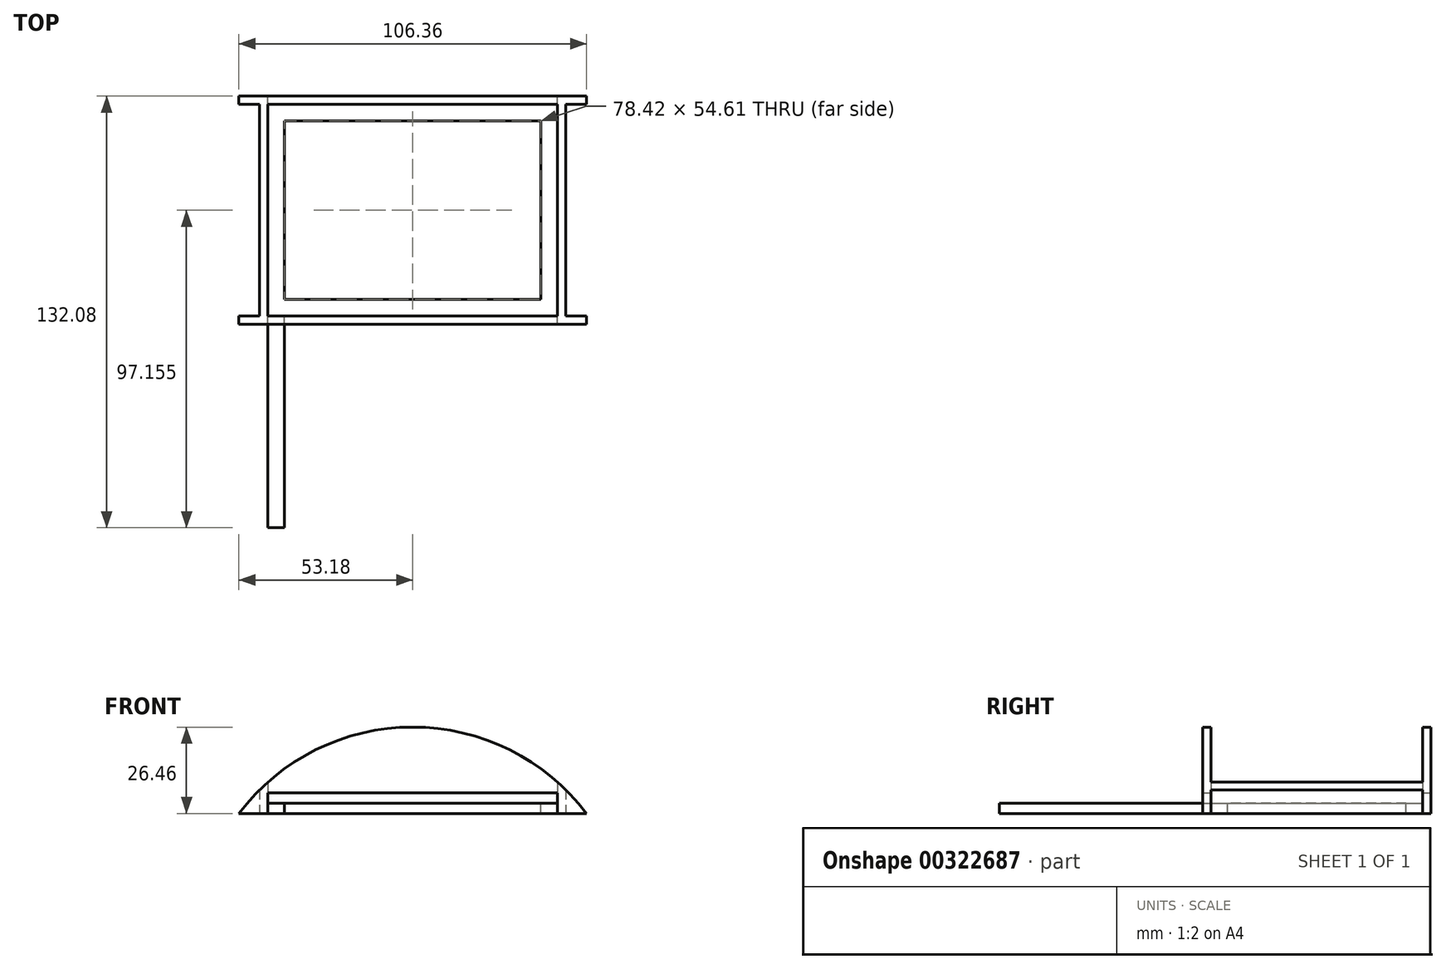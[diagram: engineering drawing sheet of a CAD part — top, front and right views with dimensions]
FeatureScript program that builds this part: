
annotation { "Feature Type Name" : "Feature", "Feature Type Description" : "" }
export const myFeature = defineFeature(function(context is Context, id is Id, definition is map)
    precondition{}
    {
        {
            var Q0;
            Q0=qCreatedBy(makeId("Front.planeOp"),FACE);
            var sketch = newSketch(context, id + "F0", { "sketchPlane" : qUnion([Q0])});
            skLineSegment(sketch, "E0", {"start": v(44.3, 0) * mm, "end": v(-44.3, 0) * mm});
            skLineSegment(sketch, "E1", {"start": v(-44.3, 0) * mm, "end": v(-44.3, 26.46) * mm});
            skLineSegment(sketch, "E2", {"start": v(44.3, 0) * mm, "end": v(44.3, 26.46) * mm});
            skLineSegment(sketch, "E3", {"start": v(-44.3, 0) * mm, "end": v(-46.83, 0) * mm});
            skLineSegment(sketch, "E4", {"start": v(-46.83, 0) * mm, "end": v(-53.18, 0) * mm});
            skLineSegment(sketch, "E5", {"start": v(-46.83, 0) * mm, "end": v(-46.83, 26.46) * mm});
            skLineSegment(sketch, "E6", {"start": v(44.3, 0) * mm, "end": v(46.83, 0) * mm});
            skLineSegment(sketch, "E7", {"start": v(46.83, 0) * mm, "end": v(46.83, 26.46) * mm});
            skLineSegment(sketch, "E8", {"start": v(-44.3, 26.46) * mm, "end": v(44.3, 26.46) * mm, "construction": true});
            skLineSegment(sketch, "E9", {"start": v(46.83, 0) * mm, "end": v(53.18, 0) * mm});
            skLineSegment(sketch, "E10", {"start": v(-46.83, 26.46) * mm, "end": v(-44.3, 26.46) * mm});
            skLineSegment(sketch, "E11", {"start": v(44.3, 26.46) * mm, "end": v(46.83, 26.46) * mm});
            skLineSegment(sketch, "E12", {"start": v(0, 0) * mm, "end": v(0, 26.46) * mm, "construction": true});
            skLineSegment(sketch, "E13", {"start": v(-53.18, 0) * mm, "end": v(-53.18, 2.54) * mm});
            skLineSegment(sketch, "E14", {"start": v(-53.18, 2.54) * mm, "end": v(-46.83, 2.54) * mm});
            skLineSegment(sketch, "E15", {"start": v(53.18, 0) * mm, "end": v(53.18, 2.54) * mm});
            skLineSegment(sketch, "E16", {"start": v(53.18, 2.54) * mm, "end": v(46.83, 2.54) * mm});
            skLineSegment(sketch, "E17", {"start": v(0, 26.46) * mm, "end": v(0, -40.22) * mm, "construction": true});
            skArc(sketch, "E18", {"start": v(0, 26.46) * mm, "mid": v(-29.7, 19.48) * mm, "end": v(-53.18, 0) * mm});
            skArc(sketch, "E19", {"start": v(0, 26.46) * mm, "mid": v(29.7, 19.48) * mm, "end": v(53.18, 0) * mm});
            skLineSegment(sketch, "E20.bottom", {"start": v(-44.3, 0) * mm, "end": v(44.3, 0) * mm});
            skLineSegment(sketch, "E20.top", {"start": v(-44.3, 6.35) * mm, "end": v(44.3, 6.35) * mm});
            skLineSegment(sketch, "E20.left", {"start": v(-44.3, 0) * mm, "end": v(-44.3, 6.35) * mm});
            skLineSegment(sketch, "E20.right", {"start": v(44.3, 0) * mm, "end": v(44.3, 6.35) * mm});
            skSolve(sketch);
        }
        {
            var Q0;
            {var subQ0=sQuery(id+"F0.wireOp",EDGE,"E4");Q0=makeQuery(id+"F0.imprint","IMPRINT",FACE,{"disambiguationData":[TD([[makeQuery(id+"F0.imprint","IMPRINT",EDGE,{"derivedFrom":subQ0}),-1.0]])]});}
            var Q1;
            {var subQ0=sQuery(id+"F0.wireOp",EDGE,"E9");Q1=makeQuery(id+"F0.imprint","IMPRINT",FACE,{"disambiguationData":[TD([[makeQuery(id+"F0.imprint","IMPRINT",EDGE,{"derivedFrom":subQ0}),1.0]])]});}
            var Q2;
            {var subQ4=sQuery(id+"F0.wireOp",EDGE,"E3");Q2=makeQuery(id+"F0.imprint","IMPRINT",FACE,{"disambiguationData":[TD([[makeQuery(id+"F0.imprint","IMPRINT",EDGE,{"derivedFrom":subQ4}),-1.0]])]});}
            var Q3;
            {var subQ5=sQuery(id+"F0.wireOp",EDGE,"E6");Q3=makeQuery(id+"F0.imprint","IMPRINT",FACE,{"disambiguationData":[TD([[makeQuery(id+"F0.imprint","IMPRINT",EDGE,{"derivedFrom":subQ5}),1.0]])]});}
            var Q4;
            Q4=makeQuery(id+"F0.imprint","IMPRINT",FACE,{"disambiguationData":[TD([[makeQuery(id+"F0.imprint","IMPRINT",EDGE,{"derivedFrom":sQuery(id+"F0.wireOp",EDGE,"E20.bottom")}),1.0]])]});
            var Q5;
            {var subQ0=sQuery(id+"F0.wireOp",EDGE,"E14");var subQ1=sQuery(id+"F0.wireOp",EDGE,"E5");var subQ2=makeQuery(id+"F0.imprint","INTERSECT",VERTEX,{"derivedFrom":[subQ1,subQ0]});Q5=makeQuery(id+"F0.imprint","IMPRINT",FACE,{"disambiguationData":[TD([[makeQuery(id+"F0.imprint","IMPRINT",EDGE,{"disambiguationData":[TD([[subQ2,-1.0]])],"derivedFrom":subQ1}),1.0]])]});}
            var Q6;
            {var subQ0=sQuery(id+"F0.wireOp",EDGE,"E16");var subQ1=sQuery(id+"F0.wireOp",EDGE,"E7");var subQ2=makeQuery(id+"F0.imprint","INTERSECT",VERTEX,{"derivedFrom":[subQ1,subQ0]});Q6=makeQuery(id+"F0.imprint","IMPRINT",FACE,{"disambiguationData":[TD([[makeQuery(id+"F0.imprint","IMPRINT",EDGE,{"disambiguationData":[TD([[subQ2,-1.0]])],"derivedFrom":subQ1}),-1.0]])]});}
            var Q7;
            {var subQ7=sQuery(id+"F0.wireOp",EDGE,"E20.top");Q7=makeQuery(id+"F0.imprint","IMPRINT",FACE,{"disambiguationData":[TD([[makeQuery(id+"F0.imprint","IMPRINT",EDGE,{"derivedFrom":subQ7}),1.0]])]});}
            extrude(context, id + "F1", {"entities" : qUnion([Q0, Q1, Q2, Q3, Q4, Q5, Q6, Q7]), "depth" : 2.54 * mm, "offsetDistance" : 25.4 * mm});
        }
        {
            var Q0;
            {var subQ0=sQuery(id+"F0.wireOp",EDGE,"E4");Q0=makeQuery(id+"F0.imprint","IMPRINT",FACE,{"disambiguationData":[TD([[makeQuery(id+"F0.imprint","IMPRINT",EDGE,{"derivedFrom":subQ0}),-1.0]])]});}
            var Q1;
            {var subQ0=sQuery(id+"F0.wireOp",EDGE,"E14");var subQ1=sQuery(id+"F0.wireOp",EDGE,"E5");var subQ2=makeQuery(id+"F0.imprint","INTERSECT",VERTEX,{"derivedFrom":[subQ1,subQ0]});Q1=makeQuery(id+"F0.imprint","IMPRINT",FACE,{"disambiguationData":[TD([[makeQuery(id+"F0.imprint","IMPRINT",EDGE,{"disambiguationData":[TD([[subQ2,-1.0]])],"derivedFrom":subQ1}),1.0]])]});}
            var Q2;
            {var subQ4=sQuery(id+"F0.wireOp",EDGE,"E3");Q2=makeQuery(id+"F0.imprint","IMPRINT",FACE,{"disambiguationData":[TD([[makeQuery(id+"F0.imprint","IMPRINT",EDGE,{"derivedFrom":subQ4}),-1.0]])]});}
            var Q3;
            Q3=makeQuery(id+"F0.imprint","IMPRINT",FACE,{"disambiguationData":[TD([[makeQuery(id+"F0.imprint","IMPRINT",EDGE,{"derivedFrom":sQuery(id+"F0.wireOp",EDGE,"E20.bottom")}),1.0]])]});
            var Q4;
            {var subQ5=sQuery(id+"F0.wireOp",EDGE,"E6");Q4=makeQuery(id+"F0.imprint","IMPRINT",FACE,{"disambiguationData":[TD([[makeQuery(id+"F0.imprint","IMPRINT",EDGE,{"derivedFrom":subQ5}),1.0]])]});}
            var Q5;
            {var subQ0=sQuery(id+"F0.wireOp",EDGE,"E16");var subQ1=sQuery(id+"F0.wireOp",EDGE,"E7");var subQ2=makeQuery(id+"F0.imprint","INTERSECT",VERTEX,{"derivedFrom":[subQ1,subQ0]});Q5=makeQuery(id+"F0.imprint","IMPRINT",FACE,{"disambiguationData":[TD([[makeQuery(id+"F0.imprint","IMPRINT",EDGE,{"disambiguationData":[TD([[subQ2,-1.0]])],"derivedFrom":subQ1}),-1.0]])]});}
            var Q6;
            {var subQ0=sQuery(id+"F0.wireOp",EDGE,"E9");Q6=makeQuery(id+"F0.imprint","IMPRINT",FACE,{"disambiguationData":[TD([[makeQuery(id+"F0.imprint","IMPRINT",EDGE,{"derivedFrom":subQ0}),1.0]])]});}
            var Q7;
            {var subQ7=sQuery(id+"F0.wireOp",EDGE,"E20.top");Q7=makeQuery(id+"F0.imprint","IMPRINT",FACE,{"disambiguationData":[TD([[makeQuery(id+"F0.imprint","IMPRINT",EDGE,{"derivedFrom":subQ7}),1.0]])]});}
            extrude(context, id + "F2", {"entities" : qUnion([Q0, Q1, Q2, Q3, Q4, Q5, Q6, Q7]), "depth" : 69.85 * mm, "hasSecondDirection" : true, "secondDirectionOppositeDirection" : false, "secondDirectionDepth" : 67.3 * mm, "offsetDistance" : 25.4 * mm});
        }
        {
            var Q0;
            {var subQ4=sQuery(id+"F0.wireOp",EDGE,"E3");Q0=makeQuery(id+"F0.imprint","IMPRINT",FACE,{"disambiguationData":[TD([[makeQuery(id+"F0.imprint","IMPRINT",EDGE,{"derivedFrom":subQ4}),-1.0]])]});}
            var Q1;
            {var subQ5=sQuery(id+"F0.wireOp",EDGE,"E6");Q1=makeQuery(id+"F0.imprint","IMPRINT",FACE,{"disambiguationData":[TD([[makeQuery(id+"F0.imprint","IMPRINT",EDGE,{"derivedFrom":subQ5}),1.0]])]});}
            extrude(context, id + "F3", {"entities" : qUnion([Q0, Q1]), "operationType" : NewBodyOperationType.ADD, "depth" : 69.85 * mm, "offsetDistance" : 25.4 * mm});
        }
        {
            var Q0;
            {var subQ0=sQuery(id+"F0.wireOp",EDGE,"E19");var subQ1=sQuery(id+"F0.wireOp",EDGE,"E18");var subQ2=sQuery(id+"F0.wireOp",EDGE,"E20.bottom");var subQ3=sQuery(id+"F0.wireOp",EDGE,"E9");var subQ4=sQuery(id+"F0.wireOp",EDGE,"E6");var subQ5=sQuery(id+"F0.wireOp",EDGE,"E4");var subQ6=sQuery(id+"F0.wireOp",EDGE,"E3");Q0=makeQuery(id+"F3.boolean.opBoolean","SPLIT",FACE,{"disambiguationData":[TD([makeQuery(id+"F3.opExtrude","SWEPT_FACE",FACE,{"disambiguationData":[OSD([sQuery(id+"F0.wireOp",EDGE,"E1"),sQuery(id+"F0.wireOp",EDGE,"E20.left")])]})])],"derivedFrom":makeQuery(id+"F1.opExtrude","CAP_FACE",FACE,{"disambiguationData":[OSD([subQ6,subQ5,subQ4,subQ3,subQ1,subQ0,subQ2])],"isStart":false})});}
            var sketch = newSketch(context, id + "F4", { "sketchPlane" : qUnion([Q0])});
            skLineSegment(sketch, "E21.bottom", {"start": v(-44.3, 0) * mm, "end": v(45.85, 0) * mm});
            skLineSegment(sketch, "E21.top", {"start": v(-44.3, 3.18) * mm, "end": v(45.85, 3.18) * mm});
            skLineSegment(sketch, "E21.left", {"start": v(-44.3, 0) * mm, "end": v(-44.3, 3.18) * mm});
            skLineSegment(sketch, "E21.right", {"start": v(45.85, 0) * mm, "end": v(45.85, 3.18) * mm});
            skSolve(sketch);
        }
        {
            var Q0;
            Q0 = qSketchRegion(id + "F4", true);
            extrude(context, id + "F5", {"entities" : qUnion([Q0]), "operationType" : NewBodyOperationType.ADD, "depth" : 5.08 * mm, "offsetDistance" : 25.4 * mm});
        }
        {
            var Q0;
            {var subQ0=sQuery(id+"F0.wireOp",EDGE,"E19");var subQ1=sQuery(id+"F0.wireOp",EDGE,"E18");var subQ2=sQuery(id+"F0.wireOp",EDGE,"E20.bottom");var subQ3=sQuery(id+"F0.wireOp",EDGE,"E9");var subQ4=sQuery(id+"F0.wireOp",EDGE,"E6");var subQ5=sQuery(id+"F0.wireOp",EDGE,"E4");var subQ6=sQuery(id+"F0.wireOp",EDGE,"E3");Q0=makeQuery(id+"F3.boolean.opBoolean","SPLIT",FACE,{"disambiguationData":[TD([makeQuery(id+"F3.opExtrude","SWEPT_FACE",FACE,{"disambiguationData":[OSD([sQuery(id+"F0.wireOp",EDGE,"E1"),sQuery(id+"F0.wireOp",EDGE,"E20.left")])]})])],"derivedFrom":makeQuery(id+"F2.opExtrude","CAP_FACE",FACE,{"disambiguationData":[OSD([subQ6,subQ5,subQ4,subQ3,subQ1,subQ0,subQ2])],"isStart":true})});}
            var sketch = newSketch(context, id + "F6", { "sketchPlane" : qUnion([Q0])});
            skLineSegment(sketch, "E22.bottom", {"start": v(-44.3, 0) * mm, "end": v(45.85, 0) * mm});
            skLineSegment(sketch, "E22.top", {"start": v(-44.3, 3.18) * mm, "end": v(45.85, 3.18) * mm});
            skLineSegment(sketch, "E22.left", {"start": v(-44.3, 0) * mm, "end": v(-44.3, 3.18) * mm});
            skLineSegment(sketch, "E22.right", {"start": v(45.85, 0) * mm, "end": v(45.85, 3.18) * mm});
            skSolve(sketch);
        }
        {
            var Q0;
            Q0 = qSketchRegion(id + "F6", true);
            extrude(context, id + "F7", {"entities" : qUnion([Q0]), "operationType" : NewBodyOperationType.ADD, "depth" : 5.08 * mm, "offsetDistance" : 25.4 * mm});
        }
        {
            var Q0;
            Q0=makeQuery(id+"F3.opExtrude","SWEPT_FACE",FACE,{"disambiguationData":[OSD([sQuery(id+"F0.wireOp",EDGE,"E1"),sQuery(id+"F0.wireOp",EDGE,"E20.left")])]});
            var sketch = newSketch(context, id + "F8", { "sketchPlane" : qUnion([Q0])});
            skLineSegment(sketch, "E23.bottom", {"start": v(-132.08, 0) * mm, "end": v(-7.62, 0) * mm});
            skLineSegment(sketch, "E23.top", {"start": v(-132.08, 3.18) * mm, "end": v(-5.08, 3.18) * mm});
            skLineSegment(sketch, "E23.left", {"start": v(-132.08, 0) * mm, "end": v(-132.08, 3.18) * mm});
            skLineSegment(sketch, "E23.right", {"start": v(-7.62, 0) * mm, "end": v(-7.62, 3.18) * mm});
            skSolve(sketch);
        }
        {
            var Q0;
            Q0=makeQuery(id+"F8.imprint","IMPRINT",FACE,{"disambiguationData":[TD([[makeQuery(id+"F8.imprint","IMPRINT",EDGE,{"derivedFrom":sQuery(id+"F8.wireOp",EDGE,"E23.bottom")}),1.0]])]});
            extrude(context, id + "F9", {"entities" : qUnion([Q0]), "operationType" : NewBodyOperationType.ADD, "depth" : 5.08 * mm, "offsetDistance" : 25.4 * mm});
        }
        {
            var Q0;
            Q0=makeQuery(id+"F3.opExtrude","SWEPT_FACE",FACE,{"disambiguationData":[OSD([sQuery(id+"F0.wireOp",EDGE,"E2"),sQuery(id+"F0.wireOp",EDGE,"E20.right")])]});
            var sketch = newSketch(context, id + "F10", { "sketchPlane" : qUnion([Q0])});
            skLineSegment(sketch, "E24.bottom", {"start": v(7.62, 3.18) * mm, "end": v(132.08, 3.18) * mm});
            skLineSegment(sketch, "E24.top", {"start": v(7.62, 0) * mm, "end": v(132.08, 0) * mm});
            skLineSegment(sketch, "E24.left", {"start": v(7.62, 3.18) * mm, "end": v(7.62, 0) * mm});
            skLineSegment(sketch, "E24.right", {"start": v(132.08, 3.18) * mm, "end": v(132.08, 0) * mm});
            skSolve(sketch);
        }
        {
            var Q0;
            {var subQ0=sQuery(id+"F10.wireOp",EDGE,"E24.left");Q0=makeQuery(id+"F10.imprint","IMPRINT",FACE,{"disambiguationData":[TD([[makeQuery(id+"F10.imprint","IMPRINT",EDGE,{"derivedFrom":subQ0}),-1.0]])]});}
            extrude(context, id + "F11", {"entities" : qUnion([Q0]), "operationType" : NewBodyOperationType.ADD, "depth" : 5.08 * mm, "offsetDistance" : 25.4 * mm});
        }
    });
